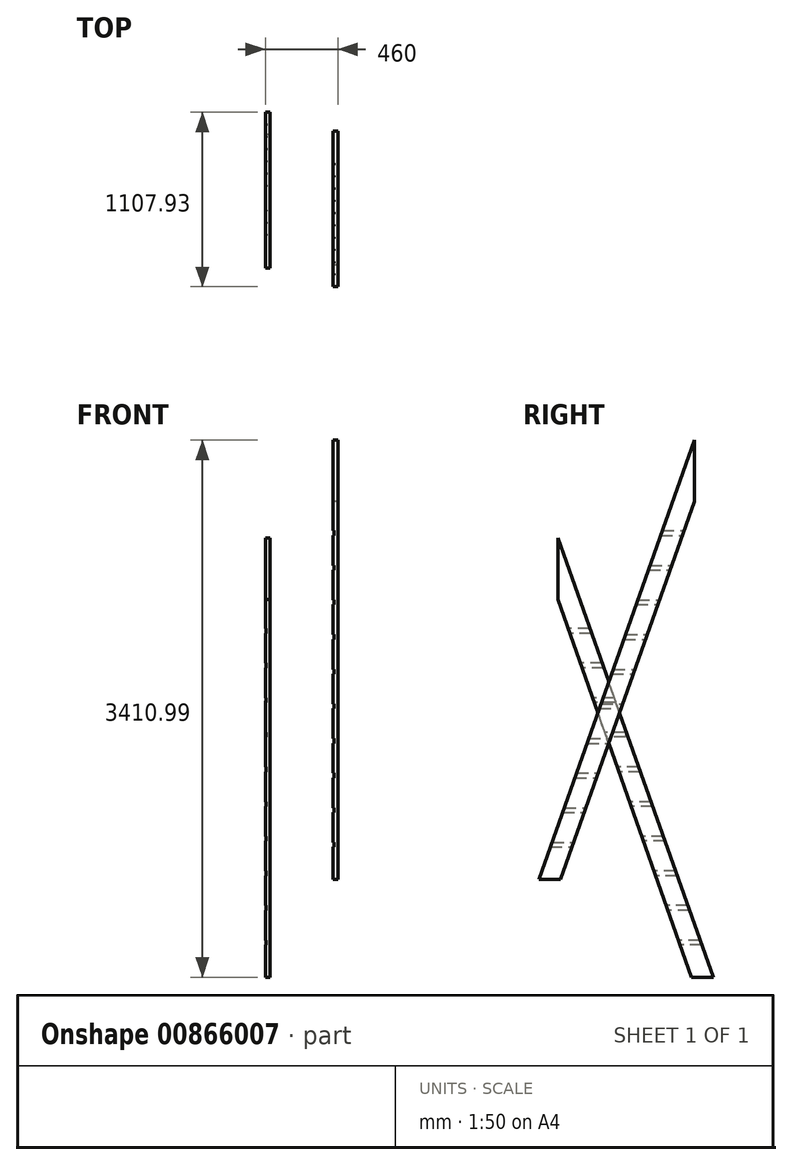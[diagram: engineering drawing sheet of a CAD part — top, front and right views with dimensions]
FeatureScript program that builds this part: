
annotation { "Feature Type Name" : "Feature", "Feature Type Description" : "" }
export const myFeature = defineFeature(function(context is Context, id is Id, definition is map)
    precondition{}
    {
        {
            var Q0;
            Q0=qCreatedBy(makeId("Right.planeOp"),FACE);
            var sketch = newSketch(context, id + "F0", { "sketchPlane" : qUnion([Q0])});
            skLineSegment(sketch, "E0", {"start": v(-137.91, 0) * mm, "end": v(850, 2789.4) * mm});
            skLineSegment(sketch, "E1", {"start": v(-137.91, 0) * mm, "end": v(0, 0) * mm});
            skLineSegment(sketch, "E2", {"start": v(0, 0) * mm, "end": v(850, 2400) * mm});
            skLineSegment(sketch, "E3", {"start": v(850, 2789.4) * mm, "end": v(850, 2400) * mm});
            skLineSegment(sketch, "E4", {"start": v(-165.89, 220) * mm, "end": v(699.37, 220) * mm, "construction": true});
            skLineSegment(sketch, "E5", {"start": v(0, 440) * mm, "end": v(906.06, 440) * mm, "construction": true});
            skLineSegment(sketch, "E6", {"start": v(-142.96, 660) * mm, "end": v(897.83, 660) * mm, "construction": true});
            skLineSegment(sketch, "E7", {"start": v(57.25, 880) * mm, "end": v(743.95, 880) * mm, "construction": true});
            skLineSegment(sketch, "E8", {"start": v(156.92, 1100) * mm, "end": v(826.5, 1100) * mm, "construction": true});
            skLineSegment(sketch, "E9", {"start": v(198.07, 1320) * mm, "end": v(853.72, 1320) * mm, "construction": true});
            skLineSegment(sketch, "E10", {"start": v(349.61, 1540) * mm, "end": v(834.5, 1540) * mm, "construction": true});
            skLineSegment(sketch, "E11", {"start": v(448.33, 1760) * mm, "end": v(854.35, 1760) * mm, "construction": true});
            skLineSegment(sketch, "E12", {"start": v(525.46, 1980) * mm, "end": v(1066.8, 1980) * mm, "construction": true});
            skLineSegment(sketch, "E13", {"start": v(1045.37, 2200) * mm, "end": v(410.61, 2200) * mm, "construction": true});
            skSolve(sketch);
        }
        {
            var Q0;
            Q0 = qSketchRegion(id + "F0", true);
            extrude(context, id + "F1", {"entities" : qUnion([Q0]), "depth" : 30 * mm, "offsetDistance" : 25 * mm});
        }
        {
            var Q0;
            Q0=makeQuery(id+"F0.imprint","IMPRINT",FACE,{"disambiguationData":[TD([[makeQuery(id+"F0.imprint","IMPRINT",EDGE,{"derivedFrom":sQuery(id+"F0.wireOp",EDGE,"E0")}),-1.0]])]});
            var sketch = newSketch(context, id + "F2", { "sketchPlane" : qUnion([Q0])});
            skLineSegment(sketch, "E14.0", {"start": v(-165.89, 220) * mm, "end": v(699.37, 220) * mm, "construction": true});
            skLineSegment(sketch, "E15.bottom", {"start": v(-86.39, 235) * mm, "end": v(163.61, 235) * mm});
            skLineSegment(sketch, "E15.top", {"start": v(-86.39, 205) * mm, "end": v(163.61, 205) * mm});
            skLineSegment(sketch, "E15.left", {"start": v(-86.39, 235) * mm, "end": v(-86.39, 205) * mm});
            skLineSegment(sketch, "E15.right", {"start": v(163.61, 235) * mm, "end": v(163.61, 205) * mm});
            skLineSegment(sketch, "E16.bottom", {"start": v(-20.84, 455) * mm, "end": v(229.16, 455) * mm});
            skLineSegment(sketch, "E16.top", {"start": v(-20.84, 425) * mm, "end": v(229.16, 425) * mm});
            skLineSegment(sketch, "E16.left", {"start": v(-20.84, 455) * mm, "end": v(-20.84, 425) * mm});
            skLineSegment(sketch, "E16.right", {"start": v(229.16, 455) * mm, "end": v(229.16, 425) * mm});
            skLineSegment(sketch, "E17.0", {"start": v(0, 440) * mm, "end": v(906.06, 440) * mm, "construction": true});
            skLineSegment(sketch, "E17.1", {"start": v(-142.96, 660) * mm, "end": v(897.83, 660) * mm, "construction": true});
            skLineSegment(sketch, "E17.2", {"start": v(57.25, 880) * mm, "end": v(743.95, 880) * mm, "construction": true});
            skLineSegment(sketch, "E18.0", {"start": v(156.92, 1100) * mm, "end": v(826.5, 1100) * mm, "construction": true});
            skLineSegment(sketch, "E18.1", {"start": v(198.07, 1320) * mm, "end": v(853.72, 1320) * mm, "construction": true});
            skLineSegment(sketch, "E18.2", {"start": v(349.61, 1540) * mm, "end": v(834.5, 1540) * mm, "construction": true});
            skLineSegment(sketch, "E18.3", {"start": v(448.33, 1760) * mm, "end": v(854.35, 1760) * mm, "construction": true});
            skLineSegment(sketch, "E18.4", {"start": v(525.46, 1980) * mm, "end": v(1066.8, 1980) * mm, "construction": true});
            skLineSegment(sketch, "E19.bottom", {"start": v(81.74, 675) * mm, "end": v(316.31, 675) * mm});
            skLineSegment(sketch, "E19.top", {"start": v(81.74, 645) * mm, "end": v(316.31, 645) * mm});
            skLineSegment(sketch, "E19.left", {"start": v(81.74, 675) * mm, "end": v(81.74, 645) * mm});
            skLineSegment(sketch, "E19.right", {"start": v(316.31, 675) * mm, "end": v(316.31, 645) * mm});
            skLineSegment(sketch, "E20.bottom", {"start": v(140.38, 895) * mm, "end": v(333.32, 895) * mm});
            skLineSegment(sketch, "E20.top", {"start": v(140.38, 865) * mm, "end": v(333.32, 865) * mm});
            skLineSegment(sketch, "E20.left", {"start": v(140.38, 895) * mm, "end": v(140.38, 865) * mm});
            skLineSegment(sketch, "E20.right", {"start": v(333.32, 895) * mm, "end": v(333.32, 865) * mm});
            skLineSegment(sketch, "E21.bottom", {"start": v(210.05, 1115) * mm, "end": v(420.57, 1115) * mm});
            skLineSegment(sketch, "E21.top", {"start": v(210.05, 1085) * mm, "end": v(420.57, 1085) * mm});
            skLineSegment(sketch, "E21.left", {"start": v(210.05, 1115) * mm, "end": v(210.05, 1085) * mm});
            skLineSegment(sketch, "E21.right", {"start": v(420.57, 1115) * mm, "end": v(420.57, 1085) * mm});
            skLineSegment(sketch, "E22.bottom", {"start": v(283.37, 1335) * mm, "end": v(662.16, 1335) * mm});
            skLineSegment(sketch, "E22.top", {"start": v(283.37, 1305) * mm, "end": v(662.16, 1305) * mm});
            skLineSegment(sketch, "E22.left", {"start": v(283.37, 1335) * mm, "end": v(283.37, 1305) * mm});
            skLineSegment(sketch, "E22.right", {"start": v(662.16, 1335) * mm, "end": v(662.16, 1305) * mm});
            skLineSegment(sketch, "E23.bottom", {"start": v(333.32, 1555) * mm, "end": v(703.12, 1555) * mm});
            skLineSegment(sketch, "E23.top", {"start": v(333.32, 1525) * mm, "end": v(703.12, 1525) * mm});
            skLineSegment(sketch, "E23.left", {"start": v(333.32, 1555) * mm, "end": v(333.32, 1525) * mm});
            skLineSegment(sketch, "E23.right", {"start": v(703.12, 1555) * mm, "end": v(703.12, 1525) * mm});
            skLineSegment(sketch, "E24.bottom", {"start": v(420.57, 1775) * mm, "end": v(760.27, 1775) * mm});
            skLineSegment(sketch, "E24.top", {"start": v(420.57, 1745) * mm, "end": v(760.27, 1745) * mm});
            skLineSegment(sketch, "E24.left", {"start": v(420.57, 1775) * mm, "end": v(420.57, 1745) * mm});
            skLineSegment(sketch, "E24.right", {"start": v(760.27, 1775) * mm, "end": v(760.27, 1745) * mm});
            skLineSegment(sketch, "E25.bottom", {"start": v(497.7, 1995) * mm, "end": v(877.54, 1995) * mm});
            skLineSegment(sketch, "E25.top", {"start": v(497.7, 1965) * mm, "end": v(877.54, 1965) * mm});
            skLineSegment(sketch, "E25.left", {"start": v(497.7, 1995) * mm, "end": v(497.7, 1965) * mm});
            skLineSegment(sketch, "E25.right", {"start": v(877.54, 1995) * mm, "end": v(877.54, 1965) * mm});
            skLineSegment(sketch, "E26.bottom", {"start": v(587.81, 2215) * mm, "end": v(849.38, 2215) * mm});
            skLineSegment(sketch, "E26.top", {"start": v(587.81, 2185) * mm, "end": v(849.38, 2185) * mm});
            skLineSegment(sketch, "E26.left", {"start": v(587.81, 2215) * mm, "end": v(587.81, 2185) * mm});
            skLineSegment(sketch, "E26.right", {"start": v(849.38, 2215) * mm, "end": v(849.38, 2185) * mm});
            skSolve(sketch);
        }
        {
            var Q0;
            Q0 = qSketchRegion(id + "F2", true);
            extrude(context, id + "F3", {"entities" : qUnion([Q0]), "operationType" : NewBodyOperationType.REMOVE, "depth" : 5 * mm, "offsetDistance" : 25 * mm});
        }
        {
            var Q0;
            {var subQ0=sQuery(id+"F0.wireOp",EDGE,"E0");var subQ1=sQuery(id+"F0.wireOp",EDGE,"E2");Q0=makeQuery(id+"F3.boolean.opBoolean","SPLIT",FACE,{"disambiguationData":[TD([makeQuery(id+"F3.opExtrude","SWEPT_FACE",FACE,{"disambiguationData":[OSD([sQuery(id+"F2.wireOp",EDGE,"E16.bottom")])]})])],"derivedFrom":makeQuery(id+"F1.opExtrude","CAP_FACE",FACE,{"disambiguationData":[OSD([subQ0,sQuery(id+"F0.wireOp",EDGE,"E1"),subQ1,sQuery(id+"F0.wireOp",EDGE,"E3")])],"isStart":true})});}
            cPlane(context, id + "F4", {"entities" : qUnion([Q0]), "cplaneType" : CPlaneType.OFFSET, "offset" : 400 * mm, "width" : 150 * mm, "height" : 150 * mm});
        }
        {
            var Q0;
            Q0=qCreatedBy(id+"F4.planeOp",FACE);
            var sketch = newSketch(context, id + "F5", { "sketchPlane" : qUnion([Q0])});
            skLineSegment(sketch, "E27", {"start": v(-970.02, -621.59) * mm, "end": v(17.9, 2167.81) * mm});
            skLineSegment(sketch, "E28", {"start": v(-970.02, -621.59) * mm, "end": v(-832.1, -621.59) * mm});
            skLineSegment(sketch, "E29", {"start": v(-832.1, -621.59) * mm, "end": v(17.9, 1778.41) * mm});
            skLineSegment(sketch, "E30", {"start": v(17.9, 2167.81) * mm, "end": v(17.9, 1778.41) * mm});
            skLineSegment(sketch, "E31", {"start": v(-998, -401.59) * mm, "end": v(-132.74, -401.59) * mm, "construction": true});
            skLineSegment(sketch, "E32", {"start": v(-832.1, -181.59) * mm, "end": v(73.95, -181.59) * mm, "construction": true});
            skLineSegment(sketch, "E33", {"start": v(-975.07, 38.41) * mm, "end": v(65.72, 38.41) * mm, "construction": true});
            skLineSegment(sketch, "E34", {"start": v(-774.86, 258.41) * mm, "end": v(-88.16, 258.41) * mm, "construction": true});
            skLineSegment(sketch, "E35", {"start": v(-675.2, 478.41) * mm, "end": v(-5.6, 478.41) * mm, "construction": true});
            skLineSegment(sketch, "E36", {"start": v(-634.04, 698.41) * mm, "end": v(21.6, 698.41) * mm, "construction": true});
            skLineSegment(sketch, "E37", {"start": v(-482.5, 918.41) * mm, "end": v(2.38, 918.41) * mm, "construction": true});
            skLineSegment(sketch, "E38", {"start": v(-383.77, 1138.41) * mm, "end": v(22.24, 1138.41) * mm, "construction": true});
            skLineSegment(sketch, "E39", {"start": v(-306.65, 1358.41) * mm, "end": v(234.7, 1358.41) * mm, "construction": true});
            skLineSegment(sketch, "E40", {"start": v(-266.32, 1578.41) * mm, "end": v(229.16, 1578.41) * mm, "construction": true});
            skSolve(sketch);
        }
        {
            var Q0;
            Q0 = qSketchRegion(id + "F5", true);
            extrude(context, id + "F6", {"entities" : qUnion([Q0]), "depth" : 30 * mm, "offsetDistance" : 25 * mm});
        }
        {
            var Q0;
            Q0=makeQuery(id+"F6.opExtrude","CAP_FACE",FACE,{"disambiguationData":[OSD([sQuery(id+"F5.wireOp",EDGE,"E27"),sQuery(id+"F5.wireOp",EDGE,"E28"),sQuery(id+"F5.wireOp",EDGE,"E29"),sQuery(id+"F5.wireOp",EDGE,"E30")])],"isStart":false});
            var sketch = newSketch(context, id + "F7", { "sketchPlane" : qUnion([Q0])});
            skLineSegment(sketch, "E41.0", {"start": v(-1195.53, -401.59) * mm, "end": v(-330.27, -401.59) * mm, "construction": true});
            skLineSegment(sketch, "E42.bottom", {"start": v(-932.68, -386.59) * mm, "end": v(-682.68, -386.59) * mm});
            skLineSegment(sketch, "E42.top", {"start": v(-932.68, -416.59) * mm, "end": v(-682.68, -416.59) * mm});
            skLineSegment(sketch, "E42.left", {"start": v(-932.68, -386.59) * mm, "end": v(-932.68, -416.59) * mm});
            skLineSegment(sketch, "E42.right", {"start": v(-682.68, -386.59) * mm, "end": v(-682.68, -416.59) * mm});
            skLineSegment(sketch, "E43.bottom", {"start": v(-861.15, -166.59) * mm, "end": v(-611.15, -166.59) * mm});
            skLineSegment(sketch, "E43.top", {"start": v(-861.15, -196.59) * mm, "end": v(-611.15, -196.59) * mm});
            skLineSegment(sketch, "E43.left", {"start": v(-861.15, -166.59) * mm, "end": v(-861.15, -196.59) * mm});
            skLineSegment(sketch, "E43.right", {"start": v(-611.15, -166.59) * mm, "end": v(-611.15, -196.59) * mm});
            skLineSegment(sketch, "E44.0", {"start": v(-1029.64, -181.59) * mm, "end": v(-123.58, -181.59) * mm, "construction": true});
            skLineSegment(sketch, "E44.1", {"start": v(-1172.6, 38.41) * mm, "end": v(-131.81, 38.41) * mm, "construction": true});
            skLineSegment(sketch, "E44.2", {"start": v(-972.4, 258.41) * mm, "end": v(-285.69, 258.41) * mm, "construction": true});
            skLineSegment(sketch, "E45.0", {"start": v(-872.72, 478.41) * mm, "end": v(-203.14, 478.41) * mm, "construction": true});
            skLineSegment(sketch, "E45.1", {"start": v(-831.57, 698.41) * mm, "end": v(-175.92, 698.41) * mm, "construction": true});
            skLineSegment(sketch, "E45.2", {"start": v(-680.03, 918.41) * mm, "end": v(-195.15, 918.41) * mm, "construction": true});
            skLineSegment(sketch, "E45.3", {"start": v(-581.3, 1138.41) * mm, "end": v(-175.29, 1138.41) * mm, "construction": true});
            skLineSegment(sketch, "E45.4", {"start": v(-504.18, 1358.41) * mm, "end": v(37.16, 1358.41) * mm, "construction": true});
            skLineSegment(sketch, "E46.bottom", {"start": v(-947.9, 53.41) * mm, "end": v(-524.9, 53.41) * mm});
            skLineSegment(sketch, "E46.top", {"start": v(-947.9, 23.41) * mm, "end": v(-524.9, 23.41) * mm});
            skLineSegment(sketch, "E46.left", {"start": v(-947.9, 53.41) * mm, "end": v(-947.9, 23.41) * mm});
            skLineSegment(sketch, "E46.right", {"start": v(-524.9, 53.41) * mm, "end": v(-524.9, 23.41) * mm});
            skLineSegment(sketch, "E47.bottom", {"start": v(-889.26, 273.41) * mm, "end": v(-413.12, 273.41) * mm});
            skLineSegment(sketch, "E47.top", {"start": v(-889.26, 243.41) * mm, "end": v(-413.12, 243.41) * mm});
            skLineSegment(sketch, "E47.left", {"start": v(-889.26, 273.41) * mm, "end": v(-889.26, 243.41) * mm});
            skLineSegment(sketch, "E47.right", {"start": v(-413.12, 273.41) * mm, "end": v(-413.12, 243.41) * mm});
            skLineSegment(sketch, "E48.bottom", {"start": v(-759.94, 493.41) * mm, "end": v(-348.46, 493.41) * mm});
            skLineSegment(sketch, "E48.top", {"start": v(-759.94, 463.41) * mm, "end": v(-348.46, 463.41) * mm});
            skLineSegment(sketch, "E48.left", {"start": v(-759.94, 493.41) * mm, "end": v(-759.94, 463.41) * mm});
            skLineSegment(sketch, "E48.right", {"start": v(-348.46, 493.41) * mm, "end": v(-348.46, 463.41) * mm});
            skLineSegment(sketch, "E49.bottom", {"start": v(-698.3, 713.41) * mm, "end": v(-274.63, 713.41) * mm});
            skLineSegment(sketch, "E49.top", {"start": v(-698.3, 683.41) * mm, "end": v(-274.63, 683.41) * mm});
            skLineSegment(sketch, "E49.left", {"start": v(-698.3, 713.41) * mm, "end": v(-698.3, 683.41) * mm});
            skLineSegment(sketch, "E49.right", {"start": v(-274.63, 713.41) * mm, "end": v(-274.63, 683.41) * mm});
            skLineSegment(sketch, "E50.bottom", {"start": v(-413.12, 933.41) * mm, "end": v(-162.13, 933.41) * mm});
            skLineSegment(sketch, "E50.top", {"start": v(-413.12, 903.41) * mm, "end": v(-162.13, 903.41) * mm});
            skLineSegment(sketch, "E50.left", {"start": v(-413.12, 933.41) * mm, "end": v(-413.12, 903.41) * mm});
            skLineSegment(sketch, "E50.right", {"start": v(-162.13, 933.41) * mm, "end": v(-162.13, 903.41) * mm});
            skLineSegment(sketch, "E51.bottom", {"start": v(-348.46, 1153.41) * mm, "end": v(-79.94, 1153.41) * mm});
            skLineSegment(sketch, "E51.top", {"start": v(-348.46, 1123.41) * mm, "end": v(-79.94, 1123.41) * mm});
            skLineSegment(sketch, "E51.left", {"start": v(-348.46, 1153.41) * mm, "end": v(-348.46, 1123.41) * mm});
            skLineSegment(sketch, "E51.right", {"start": v(-79.94, 1153.41) * mm, "end": v(-79.94, 1123.41) * mm});
            skLineSegment(sketch, "E52.bottom", {"start": v(-434.93, 1373.41) * mm, "end": v(25, 1373.41) * mm});
            skLineSegment(sketch, "E52.top", {"start": v(-434.93, 1343.41) * mm, "end": v(25, 1343.41) * mm});
            skLineSegment(sketch, "E52.left", {"start": v(-434.93, 1373.41) * mm, "end": v(-434.93, 1343.41) * mm});
            skLineSegment(sketch, "E52.right", {"start": v(25, 1373.41) * mm, "end": v(25, 1343.41) * mm});
            skSolve(sketch);
        }
        {
            var Q0;
            Q0 = qSketchRegion(id + "F7", true);
            extrude(context, id + "F8", {"entities" : qUnion([Q0]), "operationType" : NewBodyOperationType.REMOVE, "oppositeDirection" : true, "depth" : 5 * mm, "offsetDistance" : 25 * mm});
        }
        {
            var Q0;
            {var subQ0=sQuery(id+"F5.wireOp",EDGE,"E27");var subQ1=sQuery(id+"F5.wireOp",EDGE,"E30");var subQ2=sQuery(id+"F5.wireOp",EDGE,"E29");Q0=makeQuery(id+"F8.boolean.opBoolean","SPLIT",FACE,{"disambiguationData":[TD([makeQuery(id+"F6.opExtrude","SWEPT_FACE",FACE,{"disambiguationData":[OSD([subQ1])]})])],"derivedFrom":makeQuery(id+"F6.opExtrude","CAP_FACE",FACE,{"disambiguationData":[OSD([subQ0,sQuery(id+"F5.wireOp",EDGE,"E28"),subQ2,subQ1])],"isStart":false})});}
            var sketch = newSketch(context, id + "F9", { "sketchPlane" : qUnion([Q0])});
            skLineSegment(sketch, "E53.bottom", {"start": v(-235.77, 1593.41) * mm, "end": v(43.16, 1593.41) * mm});
            skLineSegment(sketch, "E53.top", {"start": v(-235.77, 1563.41) * mm, "end": v(43.16, 1563.41) * mm});
            skLineSegment(sketch, "E53.left", {"start": v(-235.77, 1593.41) * mm, "end": v(-235.77, 1563.41) * mm});
            skLineSegment(sketch, "E53.right", {"start": v(43.16, 1593.41) * mm, "end": v(43.16, 1563.41) * mm});
            skSolve(sketch);
        }
        {
            var Q0;
            Q0 = qSketchRegion(id + "F9", true);
            extrude(context, id + "F10", {"entities" : qUnion([Q0]), "operationType" : NewBodyOperationType.REMOVE, "oppositeDirection" : true, "depth" : 5 * mm, "offsetDistance" : 25 * mm});
        }
    });
